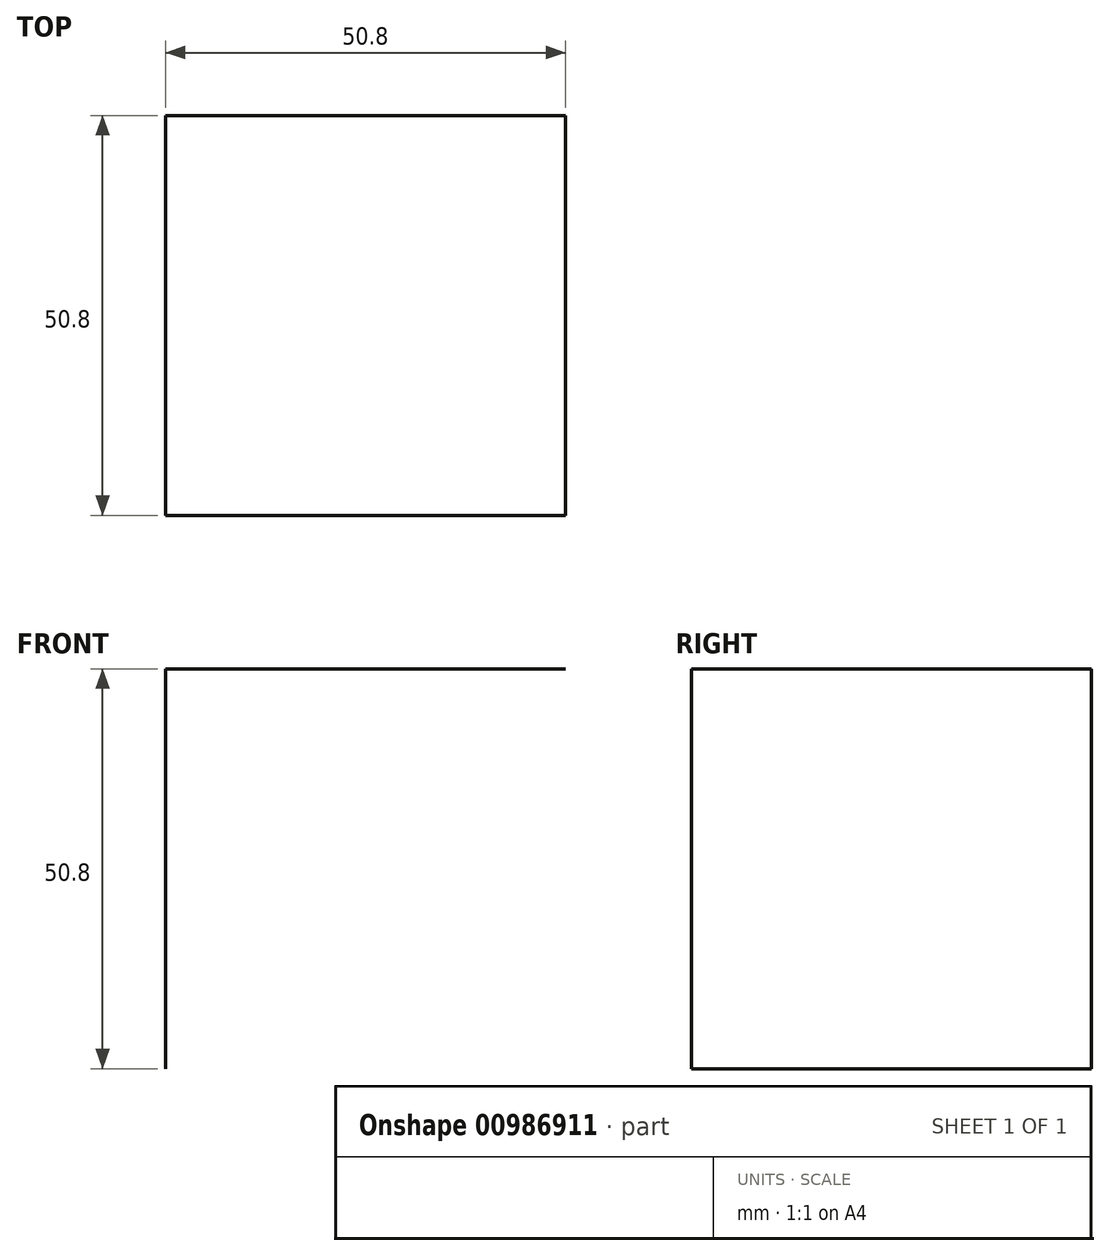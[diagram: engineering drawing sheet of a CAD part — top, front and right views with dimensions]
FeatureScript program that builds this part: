
annotation { "Feature Type Name" : "Feature", "Feature Type Description" : "" }
export const myFeature = defineFeature(function(context is Context, id is Id, definition is map)
    precondition{}
    {
        {
            var Q0;
            Q0=qCreatedBy(makeId("Front.planeOp"),FACE);
            var sketch = newSketch(context, id + "F0", { "sketchPlane" : qUnion([Q0])});
            skLineSegment(sketch, "E0.bottom", {"start": v(-44.72, 43.63) * mm, "end": v(6.08, 43.63) * mm});
            skLineSegment(sketch, "E0.top", {"start": v(-44.72, -7.17) * mm, "end": v(6.08, -7.17) * mm});
            skLineSegment(sketch, "E0.left", {"start": v(-44.72, 43.63) * mm, "end": v(-44.72, -7.17) * mm});
            skLineSegment(sketch, "E0.right", {"start": v(6.08, 43.63) * mm, "end": v(6.08, -7.17) * mm});
            skText(sketch, "E1", { "text": "Hamz", "fontName": "OpenSans-Regular.ttf"});
            const initialGuessF0  = {"E1": [-0.03914, 0.00982, 1, 0, 0.01088]};
            skSetInitialGuess(sketch, initialGuessF0);
            skSolve(sketch);
        }
        {
            var Q0;
            Q0=sQuery(id+"F0.wireOp",EDGE,"E0.bottom");
            var Q1;
            Q1=sQuery(id+"F0.wireOp",EDGE,"E0.left");
            extrude(context, id + "F1", {"bodyType" : ToolBodyType.SURFACE, "surfaceEntities" : qUnion([Q0, Q1]), "depth" : 50.8 * mm, "offsetDistance" : 25.4 * mm});
        }
    });
